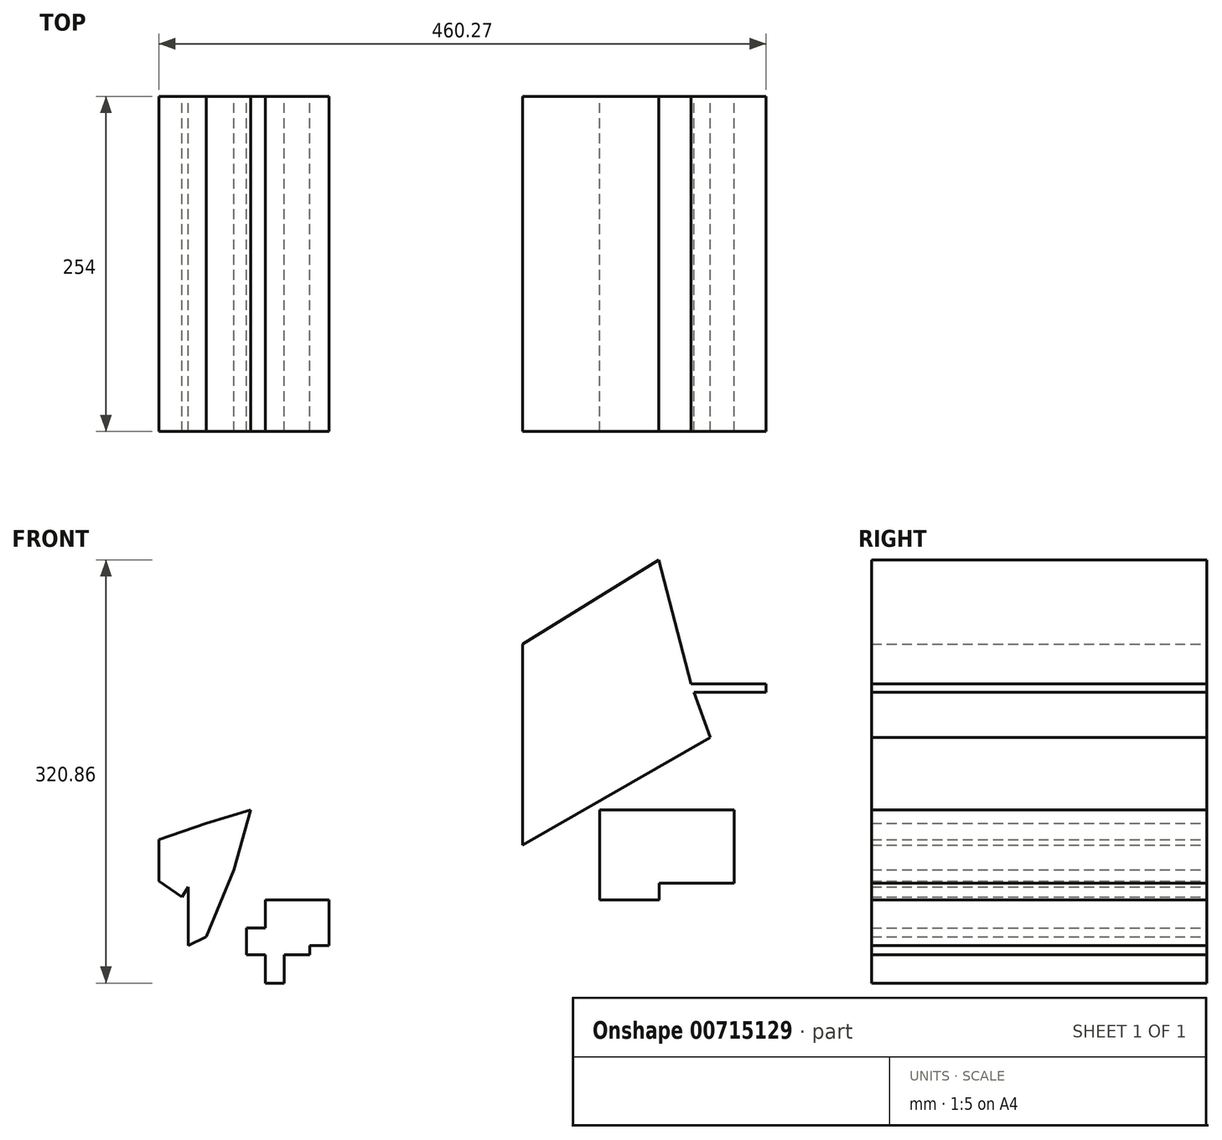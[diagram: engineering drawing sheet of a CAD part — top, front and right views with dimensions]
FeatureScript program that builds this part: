
annotation { "Feature Type Name" : "Feature", "Feature Type Description" : "" }
export const myFeature = defineFeature(function(context is Context, id is Id, definition is map)
    precondition{}
    {
        {
            var Q0;
            Q0=qCreatedBy(makeId("Front.planeOp"),FACE);
            var sketch = newSketch(context, id + "F0", { "sketchPlane" : qUnion([Q0])});
            skLineSegment(sketch, "E0", {"start": v(-231.12, -22.58) * mm, "end": v(-208.66, -58.4) * mm});
            skLineSegment(sketch, "E1", {"start": v(-208.66, -58.4) * mm, "end": v(-174.19, -45.32) * mm});
            skLineSegment(sketch, "E2", {"start": v(-174.19, -45.32) * mm, "end": v(-195.08, -96.27) * mm});
            skLineSegment(sketch, "E3", {"start": v(-195.08, -96.27) * mm, "end": v(-208.66, -58.4) * mm});
            skLineSegment(sketch, "E4", {"start": v(-208.66, -58.4) * mm, "end": v(-195.08, -10.25) * mm});
            skLineSegment(sketch, "E5", {"start": v(-195.08, -10.25) * mm, "end": v(-231.12, -22.58) * mm});
            skLineSegment(sketch, "E6", {"start": v(-196.08, -13.78) * mm, "end": v(-174.19, -45.32) * mm});
            skLineSegment(sketch, "E7", {"start": v(-195.08, -10.25) * mm, "end": v(-161.6, 0) * mm});
            skLineSegment(sketch, "E8", {"start": v(-161.6, 0) * mm, "end": v(-174.19, -45.32) * mm});
            skLineSegment(sketch, "E9", {"start": v(-231.12, -22.58) * mm, "end": v(-231.12, -53.84) * mm});
            skLineSegment(sketch, "E10", {"start": v(-231.12, -53.84) * mm, "end": v(-213.55, -65.96) * mm});
            skLineSegment(sketch, "E11", {"start": v(-213.55, -65.96) * mm, "end": v(-208.66, -58.4) * mm});
            skLineSegment(sketch, "E12", {"start": v(-208.66, -58.4) * mm, "end": v(-208.66, -102.8) * mm});
            skLineSegment(sketch, "E13", {"start": v(-208.66, -102.8) * mm, "end": v(-195.08, -96.27) * mm});
            skSolve(sketch);
        }
        {
            var Q0;
            Q0 = qSketchRegion(id + "F0", true);
            extrude(context, id + "F1", {"entities" : qUnion([Q0]), "depth" : 254 * mm, "offsetDistance" : 25.4 * mm});
        }
        {
            var Q0;
            Q0=qCreatedBy(makeId("Front.planeOp"),FACE);
            var sketch = newSketch(context, id + "F2", { "sketchPlane" : qUnion([Q0])});
            skArc(sketch, "E14", {"start": v(-103.22, 35.94) * mm, "mid": v(-106.07, 26.04) * mm, "end": v(-100.3, 17.51) * mm});
            skArc(sketch, "E15", {"start": v(-85.7, 57.34) * mm, "mid": v(-96.86, 49.66) * mm, "end": v(-85.13, 42.91) * mm});
            skArc(sketch, "E16", {"start": v(-75.79, 60.2) * mm, "mid": v(-5.83, 50.96) * mm, "end": v(-75.2, 63.87) * mm});
            skPoint(sketch, "E17", {"position": v(-131.24, -29.94) * mm});
            skPoint(sketch, "E18", {"position": v(-125.4, -29.42) * mm});
            skPoint(sketch, "E19", {"position": v(-133, -43.3) * mm});
            skPoint(sketch, "E20", {"position": v(-125.4, -43.3) * mm});
            skPoint(sketch, "E21", {"position": v(-120.15, -43.3) * mm});
            skPoint(sketch, "E22", {"position": v(-138.83, -43.3) * mm});
            skPoint(sketch, "E23", {"position": v(-113.14, -43.3) * mm});
            skPoint(sketch, "E24", {"position": v(-138.83, -35.48) * mm});
            skPoint(sketch, "E25", {"position": v(-113.14, -35.48) * mm});
            skPoint(sketch, "E26", {"position": v(-120.15, -35.48) * mm});
            skPoint(sketch, "E27", {"position": v(-120.15, -29.42) * mm});
            skPoint(sketch, "E28", {"position": v(-113.14, -22.8) * mm});
            skPoint(sketch, "E29", {"position": v(-125.4, -13.42) * mm});
            skPoint(sketch, "E30", {"position": v(-120.15, -13.42) * mm});
            skPoint(sketch, "E31", {"position": v(-113.14, -13.42) * mm});
            skPoint(sketch, "E32", {"position": v(0, -22.8) * mm});
            skPoint(sketch, "E33", {"position": v(0, 0) * mm});
            skLineSegment(sketch, "E34", {"start": v(44.46, 125.85) * mm, "end": v(172.3, 95.63) * mm});
            skLineSegment(sketch, "E35", {"start": v(172.3, 95.63) * mm, "end": v(147.78, 189.53) * mm});
            skLineSegment(sketch, "E36", {"start": v(147.78, 189.53) * mm, "end": v(44.46, 125.85) * mm});
            skLineSegment(sketch, "E37", {"start": v(172.3, 95.63) * mm, "end": v(44.46, -26.75) * mm});
            skLineSegment(sketch, "E38", {"start": v(44.46, 125.85) * mm, "end": v(44.46, -26.75) * mm});
            skLineSegment(sketch, "E39", {"start": v(172.3, 95.63) * mm, "end": v(186.9, 54.9) * mm});
            skLineSegment(sketch, "E40", {"start": v(186.9, 54.9) * mm, "end": v(44.46, -26.75) * mm});
            skLineSegment(sketch, "E41", {"start": v(234.18, 0) * mm, "end": v(186.9, 54.9) * mm});
            skLineSegment(sketch, "E42", {"start": v(234.18, 0) * mm, "end": v(114.22, 0) * mm});
            skLineSegment(sketch, "E43.bottom", {"start": v(103.08, -55.56) * mm, "end": v(148.16, -55.56) * mm});
            skLineSegment(sketch, "E43.top", {"start": v(103.08, -29.45) * mm, "end": v(148.16, -29.45) * mm});
            skLineSegment(sketch, "E43.left", {"start": v(103.08, -55.56) * mm, "end": v(103.08, -29.45) * mm});
            skLineSegment(sketch, "E43.right", {"start": v(148.16, -55.56) * mm, "end": v(148.16, -29.45) * mm});
            skLineSegment(sketch, "E44.bottom", {"start": v(148.16, -29.45) * mm, "end": v(204.87, -29.45) * mm});
            skLineSegment(sketch, "E44.top", {"start": v(148.16, 0) * mm, "end": v(204.87, 0) * mm});
            skLineSegment(sketch, "E44.left", {"start": v(148.16, -29.45) * mm, "end": v(148.16, 0) * mm});
            skLineSegment(sketch, "E44.right", {"start": v(204.87, -29.45) * mm, "end": v(204.87, 0) * mm});
            skLineSegment(sketch, "E45.top", {"start": v(103.08, 0) * mm, "end": v(148.16, 0) * mm});
            skLineSegment(sketch, "E45.left", {"start": v(103.08, -29.45) * mm, "end": v(103.08, 0) * mm});
            skLineSegment(sketch, "E46.bottom", {"start": v(204.87, -29.45) * mm, "end": v(148.16, -29.45) * mm});
            skLineSegment(sketch, "E46.top", {"start": v(204.87, -55.56) * mm, "end": v(148.16, -55.56) * mm});
            skLineSegment(sketch, "E46.left", {"start": v(204.87, -29.45) * mm, "end": v(204.87, -55.56) * mm});
            skLineSegment(sketch, "E46.right", {"start": v(148.16, -29.45) * mm, "end": v(148.16, -55.56) * mm});
            skLineSegment(sketch, "E47.top", {"start": v(103.08, -68.16) * mm, "end": v(148.16, -68.16) * mm});
            skLineSegment(sketch, "E47.left", {"start": v(103.08, -55.56) * mm, "end": v(103.08, -68.16) * mm});
            skLineSegment(sketch, "E47.right", {"start": v(148.16, -55.56) * mm, "end": v(148.16, -68.16) * mm});
            skLineSegment(sketch, "E48.bottom", {"start": v(-164.5, -89.66) * mm, "end": v(-150.45, -89.66) * mm});
            skLineSegment(sketch, "E48.top", {"start": v(-164.5, -109.84) * mm, "end": v(-150.45, -109.84) * mm});
            skLineSegment(sketch, "E48.left", {"start": v(-164.5, -89.66) * mm, "end": v(-164.5, -109.84) * mm});
            skLineSegment(sketch, "E48.right", {"start": v(-150.45, -89.66) * mm, "end": v(-150.45, -109.84) * mm});
            skLineSegment(sketch, "E49.bottom", {"start": v(-150.45, -109.84) * mm, "end": v(-135.9, -109.84) * mm});
            skLineSegment(sketch, "E49.top", {"start": v(-150.45, -131.33) * mm, "end": v(-135.9, -131.33) * mm});
            skLineSegment(sketch, "E49.left", {"start": v(-150.45, -109.84) * mm, "end": v(-150.45, -131.33) * mm});
            skLineSegment(sketch, "E49.right", {"start": v(-135.9, -109.84) * mm, "end": v(-135.9, -131.33) * mm});
            skLineSegment(sketch, "E50.bottom", {"start": v(-150.45, -89.66) * mm, "end": v(-135.9, -89.66) * mm});
            skLineSegment(sketch, "E50.top", {"start": v(-150.45, -68.16) * mm, "end": v(-135.9, -68.16) * mm});
            skLineSegment(sketch, "E50.left", {"start": v(-150.45, -89.66) * mm, "end": v(-150.45, -68.16) * mm});
            skLineSegment(sketch, "E50.right", {"start": v(-135.9, -89.66) * mm, "end": v(-135.9, -68.16) * mm});
            skLineSegment(sketch, "E51.bottom", {"start": v(-135.9, -89.66) * mm, "end": v(-116.6, -89.66) * mm});
            skLineSegment(sketch, "E51.top", {"start": v(-135.9, -109.84) * mm, "end": v(-116.6, -109.84) * mm});
            skLineSegment(sketch, "E51.left", {"start": v(-135.9, -89.66) * mm, "end": v(-135.9, -109.84) * mm});
            skLineSegment(sketch, "E51.right", {"start": v(-116.6, -89.66) * mm, "end": v(-116.6, -109.84) * mm});
            skLineSegment(sketch, "E52.bottom", {"start": v(-102.12, -102.97) * mm, "end": v(-135.9, -102.97) * mm});
            skLineSegment(sketch, "E52.top", {"start": v(-102.12, -68.16) * mm, "end": v(-135.9, -68.16) * mm});
            skLineSegment(sketch, "E52.left", {"start": v(-102.12, -102.97) * mm, "end": v(-102.12, -68.16) * mm});
            skLineSegment(sketch, "E52.right", {"start": v(-135.9, -102.97) * mm, "end": v(-135.9, -68.16) * mm});
            skLineSegment(sketch, "E53.bottom", {"start": v(172.3, 95.63) * mm, "end": v(229.15, 95.63) * mm});
            skLineSegment(sketch, "E53.top", {"start": v(172.3, 89.23) * mm, "end": v(229.15, 89.23) * mm});
            skLineSegment(sketch, "E53.left", {"start": v(172.3, 95.63) * mm, "end": v(172.3, 89.23) * mm});
            skLineSegment(sketch, "E53.right", {"start": v(229.15, 95.63) * mm, "end": v(229.15, 89.23) * mm});
            skSolve(sketch);
        }
        {
            var Q0;
            Q0 = qSketchRegion(id + "F2", true);
            extrude(context, id + "F3", {"entities" : qUnion([Q0]), "depth" : 254 * mm, "offsetDistance" : 25.4 * mm});
        }
    });
